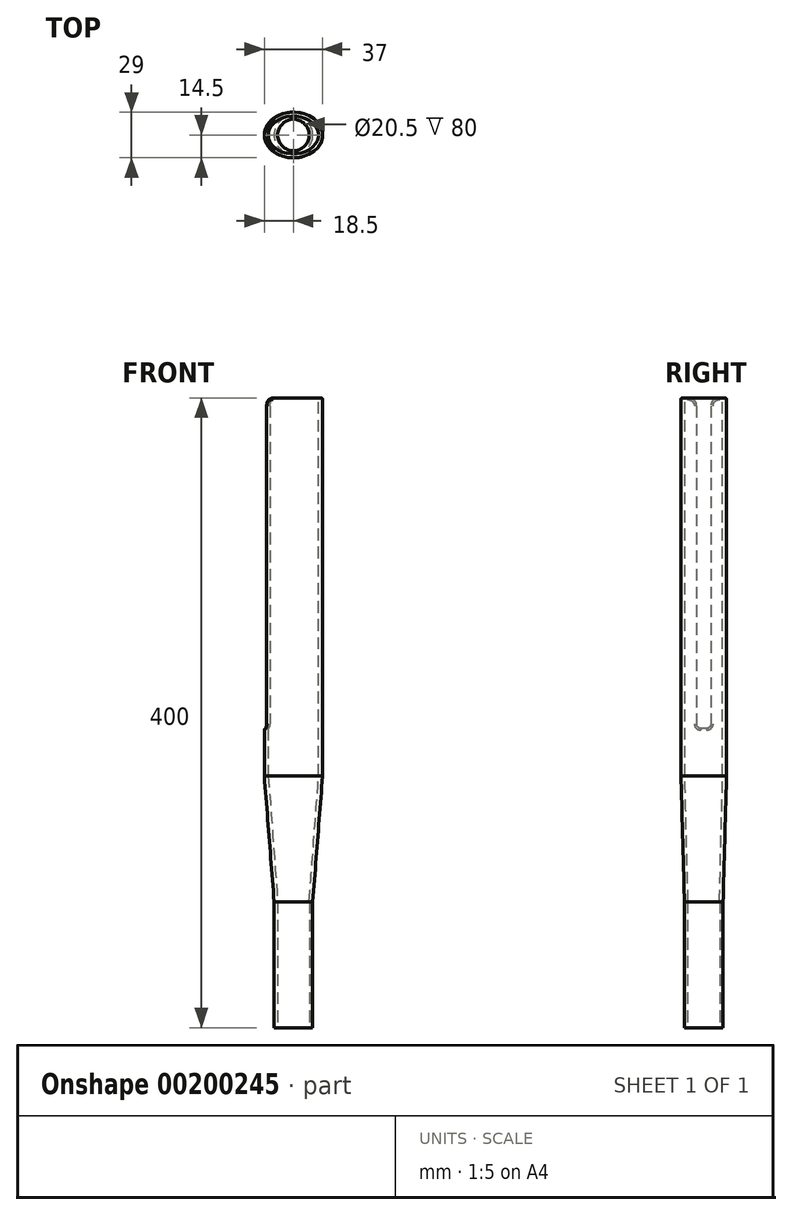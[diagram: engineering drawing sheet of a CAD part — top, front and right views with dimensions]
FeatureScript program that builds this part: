
annotation { "Feature Type Name" : "Feature", "Feature Type Description" : "" }
export const myFeature = defineFeature(function(context is Context, id is Id, definition is map)
    precondition{}
    {
        {
            var Q0;
            Q0=qCreatedBy(makeId("Top.planeOp"),FACE);
            var sketch = newSketch(context, id + "F0", { "sketchPlane" : qUnion([Q0])});
            skCircle(sketch, "E0", {"center": v(0, 0) * mm, "radius": 12.25 * mm});
            skSolve(sketch);
        }
        {
            var Q0;
            Q0 = qSketchRegion(id + "F0", true);
            extrude(context, id + "F1", {"entities" : qUnion([Q0]), "depth" : 80 * mm});
        }
        {
            var Q0;
            Q0=qCreatedBy(makeId("Top.planeOp"),FACE);
            cPlane(context, id + "F2", {"entities" : qUnion([Q0]), "cplaneType" : CPlaneType.OFFSET, "offset" : 160 * mm, "width" : 150 * mm, "height" : 150 * mm});
        }
        {
            var Q0;
            Q0=qCreatedBy(id+"F2.planeOp",FACE);
            var sketch = newSketch(context, id + "F3", { "sketchPlane" : qUnion([Q0])});
            skEllipse(sketch, "E1", {"center": v(0, 0) * mm, "majorRadius": 18.5 * mm, "minorRadius": 14.5 * mm, "majorAxis": v(-1, 0)});
            skSolve(sketch);
        }
        {
            var Q0;
            Q0=makeQuery(id+"F1.opExtrude","CAP_FACE",FACE,{"disambiguationData":[OSD([sQuery(id+"F0.wireOp",EDGE,"E0")])],"isStart":false});
            var Q1;
            Q1=makeQuery(id+"F3.imprint","IMPRINT",FACE,{"disambiguationData":[TD([[makeQuery(id+"F3.imprint","IMPRINT",EDGE,{"derivedFrom":sQuery(id+"F3.wireOp",EDGE,"E1")}),1.0]])]});
            loft(context, id + "F4", {"sheetProfilesArray" : [{ "sheetProfileEntities" : qUnion([Q0]) }, { "sheetProfileEntities" : qUnion([Q1]) }]});
        }
        {
            var Q0;
            Q0=makeQuery(id+"F4.opLoft","CAP_FACE",FACE,{"disambiguationData":[OSD([makeQuery(id+"F3.imprint","IMPRINT",FACE,{"disambiguationData":[TD([[makeQuery(id+"F3.imprint","IMPRINT",EDGE,{"derivedFrom":sQuery(id+"F3.wireOp",EDGE,"E1")}),1.0]])]})])],"isStart":true});
            var sketch = newSketch(context, id + "F5", { "sketchPlane" : qUnion([Q0])});
            skEllipse(sketch, "E2", {"center": v(0, 0) * mm, "majorRadius": 16 * mm, "minorRadius": 12 * mm, "majorAxis": v(-1, 0)});
            skSolve(sketch);
        }
        {
            var Q0;
            Q0=makeQuery(id+"F1.opExtrude","CAP_FACE",FACE,{"disambiguationData":[OSD([sQuery(id+"F0.wireOp",EDGE,"E0")])],"isStart":false});
            var sketch = newSketch(context, id + "F6", { "sketchPlane" : qUnion([Q0])});
            skCircle(sketch, "E3", {"center": v(0, 0) * mm, "radius": 10 * mm});
            skSolve(sketch);
        }
        {
            var Q0;
            Q0=makeQuery(id+"F1.opExtrude","CAP_FACE",FACE,{"disambiguationData":[OSD([sQuery(id+"F0.wireOp",EDGE,"E0")])],"isStart":true});
            var sketch = newSketch(context, id + "F7", { "sketchPlane" : qUnion([Q0])});
            skCircle(sketch, "E4", {"center": v(0, 0) * mm, "radius": 10.25 * mm});
            skSolve(sketch);
        }
        {
            var Q0;
            Q0 = qSketchRegion(id + "F7", true);
            extrude(context, id + "F8", {"entities" : qUnion([Q0]), "operationType" : NewBodyOperationType.REMOVE, "oppositeDirection" : true, "depth" : 80 * mm});
        }
        {
            var Q1;
            Q1=makeQuery(id+"F5.imprint","IMPRINT",FACE,{"disambiguationData":[TD([[makeQuery(id+"F5.imprint","IMPRINT",EDGE,{"derivedFrom":sQuery(id+"F5.wireOp",EDGE,"E2")}),1.0]])]});
            var Q2;
            Q2 = qSketchRegion(id + "F6", true);
            loft(context, id + "F9", {"operationType" : NewBodyOperationType.REMOVE, "sheetProfilesArray" : [{ "sheetProfileEntities" : qUnion([Q1]) }, { "sheetProfileEntities" : qUnion([Q2]) }]});
        }
        {
            var Q0;
            Q0=qCreatedBy(id+"F2.planeOp",FACE);
            var sketch = newSketch(context, id + "F10", { "sketchPlane" : qUnion([Q0])});
            skEllipse(sketch, "E5", {"center": v(0, 0) * mm, "majorRadius": 18.5 * mm, "minorRadius": 14.5 * mm, "majorAxis": v(-1, 0)});
            skEllipse(sketch, "E6", {"center": v(0, 0) * mm, "majorRadius": 16 * mm, "minorRadius": 12 * mm, "majorAxis": v(-1, 0)});
            skSolve(sketch);
        }
        {
            var Q0;
            Q0 = qSketchRegion(id + "F10", true);
            extrude(context, id + "F11", {"entities" : qUnion([Q0]), "operationType" : NewBodyOperationType.ADD, "depth" : 240 * mm});
        }
        {
            var Q0;
            Q0=qCreatedBy(makeId("Right.planeOp"),FACE);
            var sketch = newSketch(context, id + "F12", { "sketchPlane" : qUnion([Q0])});
            skLineSegment(sketch, "E7", {"start": v(0, 0) * mm, "end": v(0, 190) * mm, "construction": true});
            skLineSegment(sketch, "E8", {"start": v(0, 190) * mm, "end": v(-4.5, 190) * mm});
            skLineSegment(sketch, "E9", {"start": v(-4.5, 190) * mm, "end": v(-4.5, 420) * mm});
            skLineSegment(sketch, "E10", {"start": v(-4.5, 420) * mm, "end": v(4.5, 420) * mm});
            skLineSegment(sketch, "E11", {"start": v(4.5, 420) * mm, "end": v(4.5, 190) * mm});
            skLineSegment(sketch, "E12", {"start": v(4.5, 190) * mm, "end": v(0, 190) * mm});
            skSolve(sketch);
        }
        {
            var Q0;
            Q0=makeQuery(id+"F1.opExtrude","SWEPT_BODY",BODY,{"disambiguationData":[OSD([sQuery(id+"F0.wireOp",EDGE,"E0")])]});
            var Q1;
            Q1=sQuery(id+"F12.wireOp",EDGE,"E7");
            transform(context, id + "F13", {"entities" : qUnion([Q0]), "transformType" : TransformType.ROTATION, "transformAxis" : qUnion([Q1]), "angle" : 90 * degree, "makeCopy" : false});
        }
        {
            var Q0;
            Q0 = qSketchRegion(id + "F12", true);
            extrude(context, id + "F14", {"entities" : qUnion([Q0]), "operationType" : NewBodyOperationType.REMOVE, "oppositeDirection" : true, "depth" : 25 * mm});
        }
        {
            var Q0;
            Q0=makeQuery(id+"F14.boolean.opBoolean","COPY",EDGE,{"derivedFrom":makeQuery(id+"F14.opExtrude","SWEPT_EDGE",EDGE,{"disambiguationData":[OSD([sQuery(id+"F12.wireOp",EDGE,"E8"),sQuery(id+"F12.wireOp",EDGE,"E9")])]})});
            var Q1;
            Q1=makeQuery(id+"F14.boolean.opBoolean","COPY",EDGE,{"derivedFrom":makeQuery(id+"F14.opExtrude","SWEPT_EDGE",EDGE,{"disambiguationData":[OSD([sQuery(id+"F12.wireOp",EDGE,"E11"),sQuery(id+"F12.wireOp",EDGE,"E12")])]})});
            fillet(context, id + "F15", {"entities" : qUnion([Q0, Q1]), "radius" : 3 * mm, "tangentPropagation" : true, "allowEdgeOverflow" : false});
        }
        {
            var Q0;
            Q0=makeQuery(id+"F14.boolean.opBoolean","INTERSECT",EDGE,{"derivedFrom":[makeQuery(id+"F11.opExtrude","CAP_FACE",FACE,{"disambiguationData":[OSD([sQuery(id+"F10.wireOp",EDGE,"E5"),sQuery(id+"F10.wireOp",EDGE,"E6")])],"isStart":false}),makeQuery(id+"F14.opExtrude","SWEPT_FACE",FACE,{"disambiguationData":[OSD([sQuery(id+"F12.wireOp",EDGE,"E11")])]})]});
            var Q1;
            Q1=makeQuery(id+"F14.boolean.opBoolean","INTERSECT",EDGE,{"derivedFrom":[makeQuery(id+"F11.opExtrude","CAP_FACE",FACE,{"disambiguationData":[OSD([sQuery(id+"F10.wireOp",EDGE,"E5"),sQuery(id+"F10.wireOp",EDGE,"E6")])],"isStart":false}),makeQuery(id+"F14.opExtrude","SWEPT_FACE",FACE,{"disambiguationData":[OSD([sQuery(id+"F12.wireOp",EDGE,"E9")])]})]});
            fillet(context, id + "F16", {"entities" : qUnion([Q0, Q1]), "radius" : 5 * mm, "tangentPropagation" : true, "allowEdgeOverflow" : false});
        }
        {
            var Q0;
            Q0=makeQuery(id+"F11.opExtrude","CAP_EDGE",EDGE,{"disambiguationData":[OSD([sQuery(id+"F10.wireOp",EDGE,"E5")])],"isStart":false});
            fillet(context, id + "F17", {"entities" : qUnion([Q0]), "radius" : 1 * mm, "tangentPropagation" : true, "allowEdgeOverflow" : false});
        }
    });
